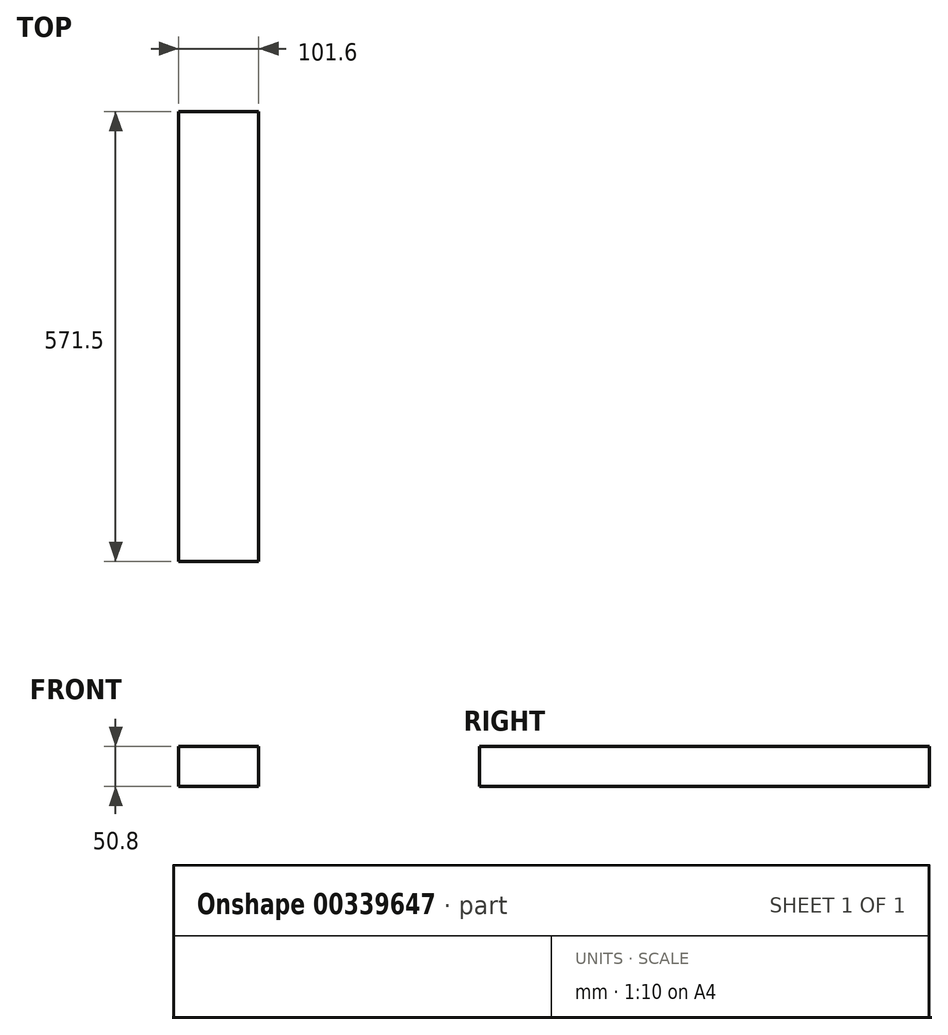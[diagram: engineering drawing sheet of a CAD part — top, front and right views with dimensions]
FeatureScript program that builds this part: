
annotation { "Feature Type Name" : "Feature", "Feature Type Description" : "" }
export const myFeature = defineFeature(function(context is Context, id is Id, definition is map)
    precondition{}
    {
        {
            var Q0;
            Q0=qCreatedBy(makeId("Front.planeOp"),FACE);
            var sketch = newSketch(context, id + "F0", { "sketchPlane" : qUnion([Q0])});
            skLineSegment(sketch, "E0.bottom", {"start": v(50.8, 25.4) * mm, "end": v(-50.8, 25.4) * mm});
            skLineSegment(sketch, "E0.top", {"start": v(50.8, -25.4) * mm, "end": v(-50.8, -25.4) * mm});
            skLineSegment(sketch, "E0.left", {"start": v(50.8, 25.4) * mm, "end": v(50.8, -25.4) * mm});
            skLineSegment(sketch, "E0.right", {"start": v(-50.8, 25.4) * mm, "end": v(-50.8, -25.4) * mm});
            skPoint(sketch, "E0.middle", {"position": v(0, 0) * mm});
            skSolve(sketch);
        }
        {
            var Q0;
            Q0=makeQuery(id+"F0.imprint","IMPRINT",FACE,{"disambiguationData":[TD([[makeQuery(id+"F0.imprint","IMPRINT",EDGE,{"derivedFrom":sQuery(id+"F0.wireOp",EDGE,"E0.bottom")}),1.0]])]});
            extrude(context, id + "F1", {"entities" : qUnion([Q0]), "depth" : 571.5 * mm});
        }
    });
